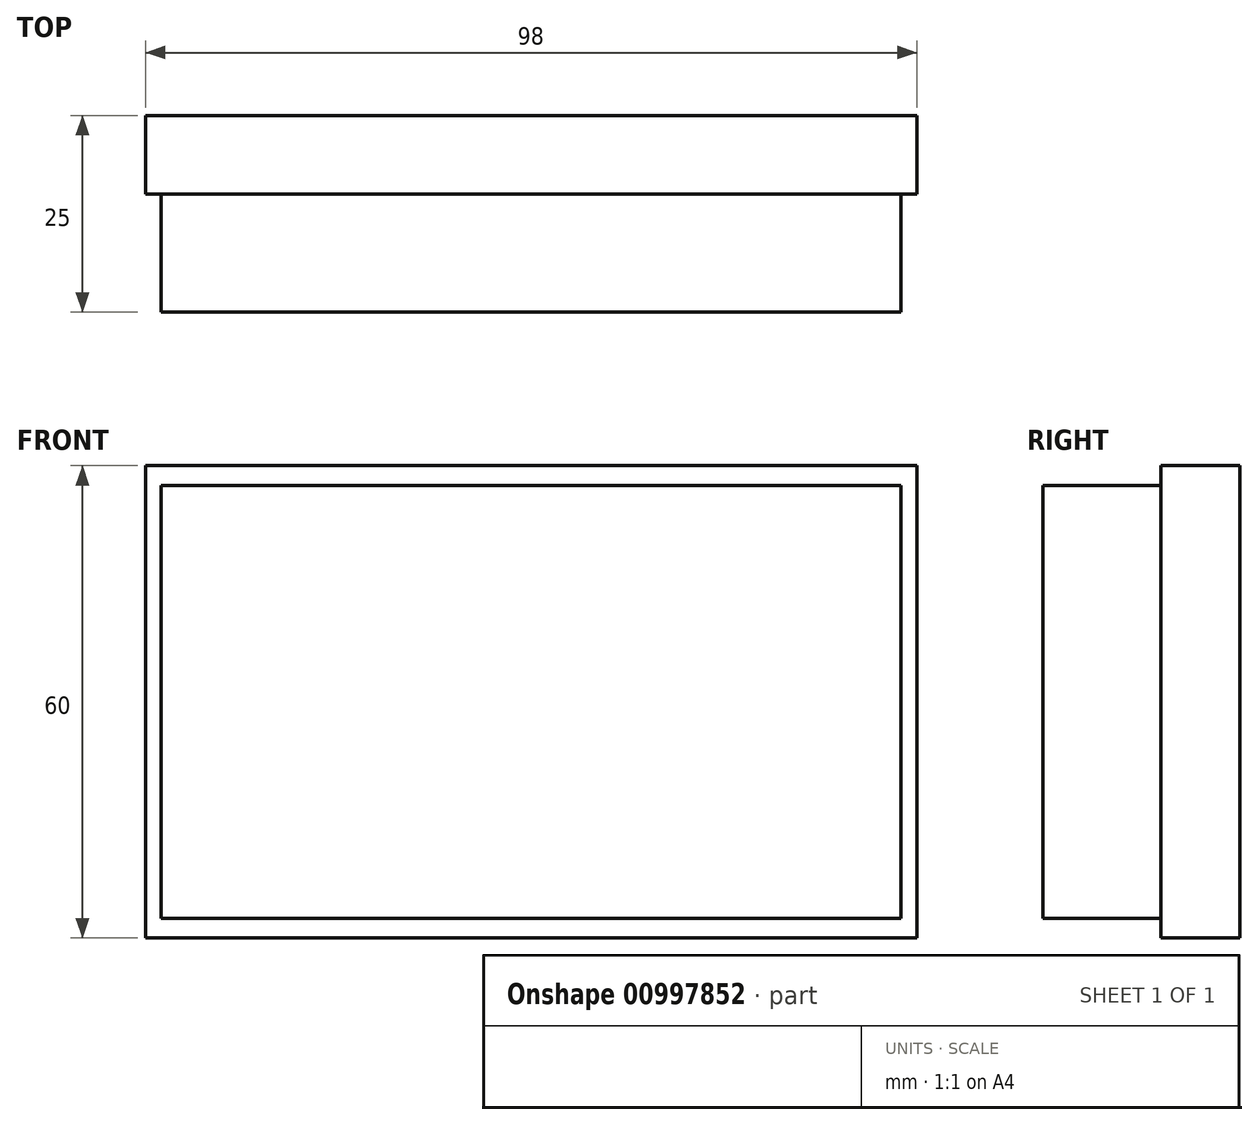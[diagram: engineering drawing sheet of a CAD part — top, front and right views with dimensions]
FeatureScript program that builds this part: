
annotation { "Feature Type Name" : "Feature", "Feature Type Description" : "" }
export const myFeature = defineFeature(function(context is Context, id is Id, definition is map)
    precondition{}
    {
        {
            var Q0;
            Q0=qCreatedBy(makeId("Front.planeOp"),FACE);
            var sketch = newSketch(context, id + "F0", { "sketchPlane" : qUnion([Q0])});
            skLineSegment(sketch, "E0.bottom", {"start": v(-49, 30) * mm, "end": v(49, 30) * mm});
            skLineSegment(sketch, "E0.top", {"start": v(-49, -30) * mm, "end": v(49, -30) * mm});
            skLineSegment(sketch, "E0.left", {"start": v(-49, 30) * mm, "end": v(-49, -30) * mm});
            skLineSegment(sketch, "E0.right", {"start": v(49, 30) * mm, "end": v(49, -30) * mm});
            skLineSegment(sketch, "E1.bottom", {"start": v(-47, 27.5) * mm, "end": v(47, 27.5) * mm});
            skLineSegment(sketch, "E1.top", {"start": v(-47, -27.5) * mm, "end": v(47, -27.5) * mm});
            skLineSegment(sketch, "E1.left", {"start": v(-47, 27.5) * mm, "end": v(-47, -27.5) * mm});
            skLineSegment(sketch, "E1.right", {"start": v(47, 27.5) * mm, "end": v(47, -27.5) * mm});
            skSolve(sketch);
        }
        {
            var Q0;
            Q0=makeQuery(id+"F0.imprint","IMPRINT",FACE,{"disambiguationData":[TD([[makeQuery(id+"F0.imprint","IMPRINT",EDGE,{"derivedFrom":sQuery(id+"F0.wireOp",EDGE,"E1.bottom")}),-1.0]])]});
            extrude(context, id + "F1", {"entities" : qUnion([Q0]), "depth" : 25 * mm, "offsetDistance" : 25 * mm});
        }
        {
            var Q0;
            Q0 = qSketchRegion(id + "F0", true);
            extrude(context, id + "F2", {"entities" : qUnion([Q0]), "operationType" : NewBodyOperationType.ADD, "depth" : 10 * mm, "offsetDistance" : 25 * mm});
        }
    });
